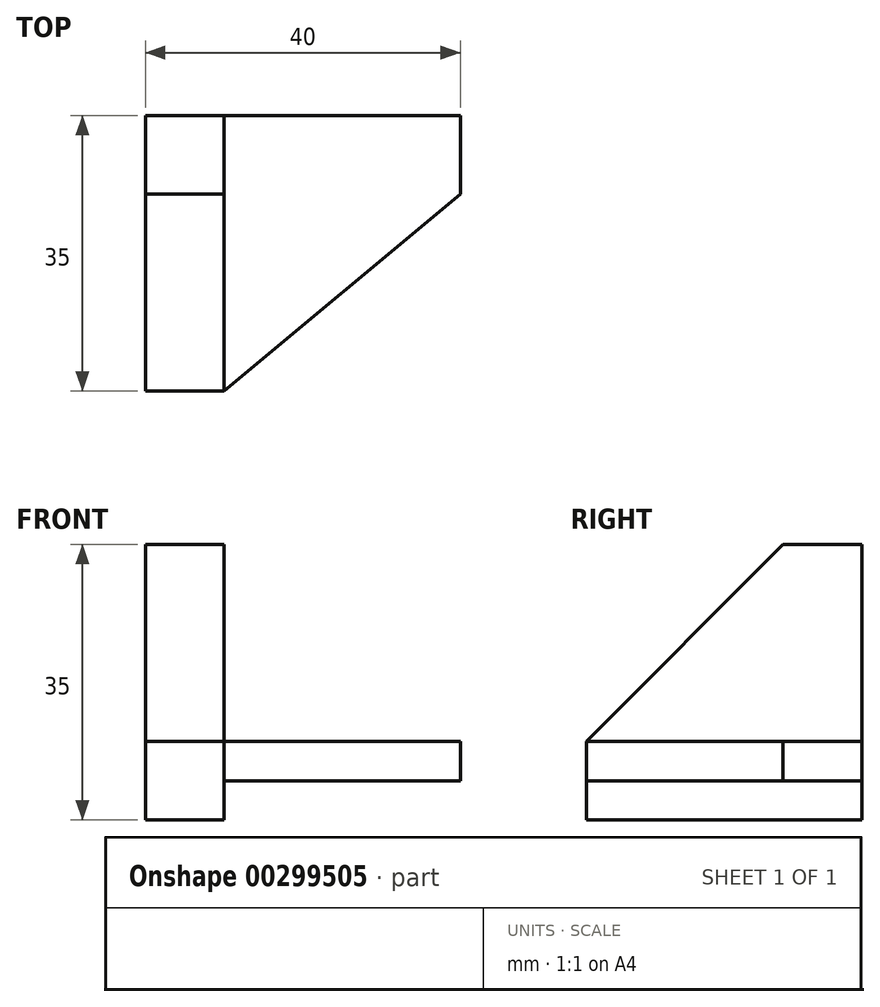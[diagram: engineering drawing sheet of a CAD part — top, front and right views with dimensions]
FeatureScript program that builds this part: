
annotation { "Feature Type Name" : "Feature", "Feature Type Description" : "" }
export const myFeature = defineFeature(function(context is Context, id is Id, definition is map)
    precondition{}
    {
        {
            var Q0;
            Q0=qCreatedBy(makeId("Front.planeOp"),FACE);
            var sketch = newSketch(context, id + "F0", { "sketchPlane" : qUnion([Q0])});
            skLineSegment(sketch, "E0.bottom", {"start": v(-32.5, 20) * mm, "end": v(32.5, 20) * mm});
            skLineSegment(sketch, "E0.top", {"start": v(-32.5, -20) * mm, "end": v(32.5, -20) * mm});
            skLineSegment(sketch, "E0.left", {"start": v(-32.5, 20) * mm, "end": v(-32.5, -20) * mm});
            skLineSegment(sketch, "E0.right", {"start": v(32.5, 20) * mm, "end": v(32.5, -20) * mm});
            skPoint(sketch, "E0.middle", {"position": v(0, 0) * mm});
            skLineSegment(sketch, "E1", {"start": v(-7.5, 20) * mm, "end": v(32.5, 0) * mm});
            skLineSegment(sketch, "E2.bottom", {"start": v(-32.5, 15) * mm, "end": v(-22.5, 15) * mm});
            skLineSegment(sketch, "E2.top", {"start": v(-32.5, -20) * mm, "end": v(-22.5, -20) * mm});
            skLineSegment(sketch, "E2.left", {"start": v(-32.5, 15) * mm, "end": v(-32.5, -20) * mm});
            skLineSegment(sketch, "E2.right", {"start": v(-22.5, 15) * mm, "end": v(-22.5, -20) * mm});
            skLineSegment(sketch, "E3.bottom", {"start": v(-22.5, -15) * mm, "end": v(7.5, -15) * mm});
            skLineSegment(sketch, "E3.top", {"start": v(-22.5, -10) * mm, "end": v(7.5, -10) * mm});
            skLineSegment(sketch, "E3.left", {"start": v(-22.5, -15) * mm, "end": v(-22.5, -10) * mm});
            skLineSegment(sketch, "E3.right", {"start": v(7.5, -15) * mm, "end": v(7.5, -10) * mm});
            skSolve(sketch);
        }
        {
            var Q0;
            {var subQ6=sQuery(id+"F0.wireOp",EDGE,"E0.top");Q0=makeQuery(id+"F0.imprint","IMPRINT",FACE,{"disambiguationData":[TD([[makeQuery(id+"F0.imprint","IMPRINT",EDGE,{"derivedFrom":subQ6}),1.0]])]});}
            extrude(context, id + "F1", {"entities" : qUnion([Q0]), "depth" : 10 * mm});
        }
        {
            var Q0;
            {var subQ1=sQuery(id+"F0.wireOp",EDGE,"E2.bottom");Q0=makeQuery(id+"F0.imprint","IMPRINT",FACE,{"disambiguationData":[TD([[makeQuery(id+"F0.imprint","IMPRINT",EDGE,{"derivedFrom":subQ1}),-1.0]])]});}
            var Q1;
            Q1=makeQuery(id+"F0.imprint","IMPRINT",FACE,{"disambiguationData":[TD([[makeQuery(id+"F0.imprint","IMPRINT",EDGE,{"derivedFrom":sQuery(id+"F0.wireOp",EDGE,"E3.bottom")}),1.0]])]});
            extrude(context, id + "F2", {"entities" : qUnion([Q0, Q1]), "operationType" : NewBodyOperationType.ADD, "depth" : 35 * mm});
        }
        {
            var Q0;
            Q0=makeQuery(id+"F2.opExtrude","SWEPT_FACE",FACE,{"disambiguationData":[OSD([sQuery(id+"F0.wireOp",EDGE,"E3.top")])]});
            var sketch = newSketch(context, id + "F3", { "sketchPlane" : qUnion([Q0])});
            skLineSegment(sketch, "E4", {"start": v(-22.5, -35) * mm, "end": v(7.5, -10) * mm});
            skSolve(sketch);
        }
        {
            var Q0;
            Q0=makeQuery(id+"F3.imprint","IMPRINT",FACE,{"disambiguationData":[TD([[makeQuery(id+"F3.imprint","IMPRINT",EDGE,{"derivedFrom":sQuery(id+"F3.wireOp",EDGE,"E4")}),-1.0]])]});
            extrude(context, id + "F4", {"entities" : qUnion([Q0]), "operationType" : NewBodyOperationType.REMOVE, "endBound" : BoundingType.THROUGH_ALL, "oppositeDirection" : true, "depth" : 25 * mm});
        }
        {
            var Q0;
            {var subQ0=sQuery(id+"F0.wireOp",EDGE,"E2.right");Q0=makeQuery(id+"F2.opExtrude","SWEPT_FACE",FACE,{"disambiguationData":[OSD([subQ0]),TDD([makeQuery(id+"F0.imprint","IMPRINT",EDGE,{"disambiguationData":[TD([[makeQuery(id+"F0.imprint","INTERSECT",VERTEX,{"derivedFrom":[sQuery(id+"F0.wireOp",EDGE,"E2.bottom"),subQ0]}),-1.0]])],"derivedFrom":subQ0})])]});}
            var sketch = newSketch(context, id + "F5", { "sketchPlane" : qUnion([Q0])});
            skLineSegment(sketch, "E5", {"start": v(-35, -10) * mm, "end": v(-10, 15) * mm});
            skSolve(sketch);
        }
        {
            var Q0;
            Q0 = qSketchRegion(id + "F5", true);
            var Q1;
            Q1=makeQuery(id+"F5.imprint","IMPRINT",FACE,{"disambiguationData":[TD([[makeQuery(id+"F5.imprint","IMPRINT",EDGE,{"derivedFrom":sQuery(id+"F5.wireOp",EDGE,"E5")}),1.0]])]});
            extrude(context, id + "F6", {"entities" : qUnion([Q0, Q1]), "operationType" : NewBodyOperationType.REMOVE, "endBound" : BoundingType.THROUGH_ALL, "oppositeDirection" : true, "depth" : 10 * mm});
        }
    });
